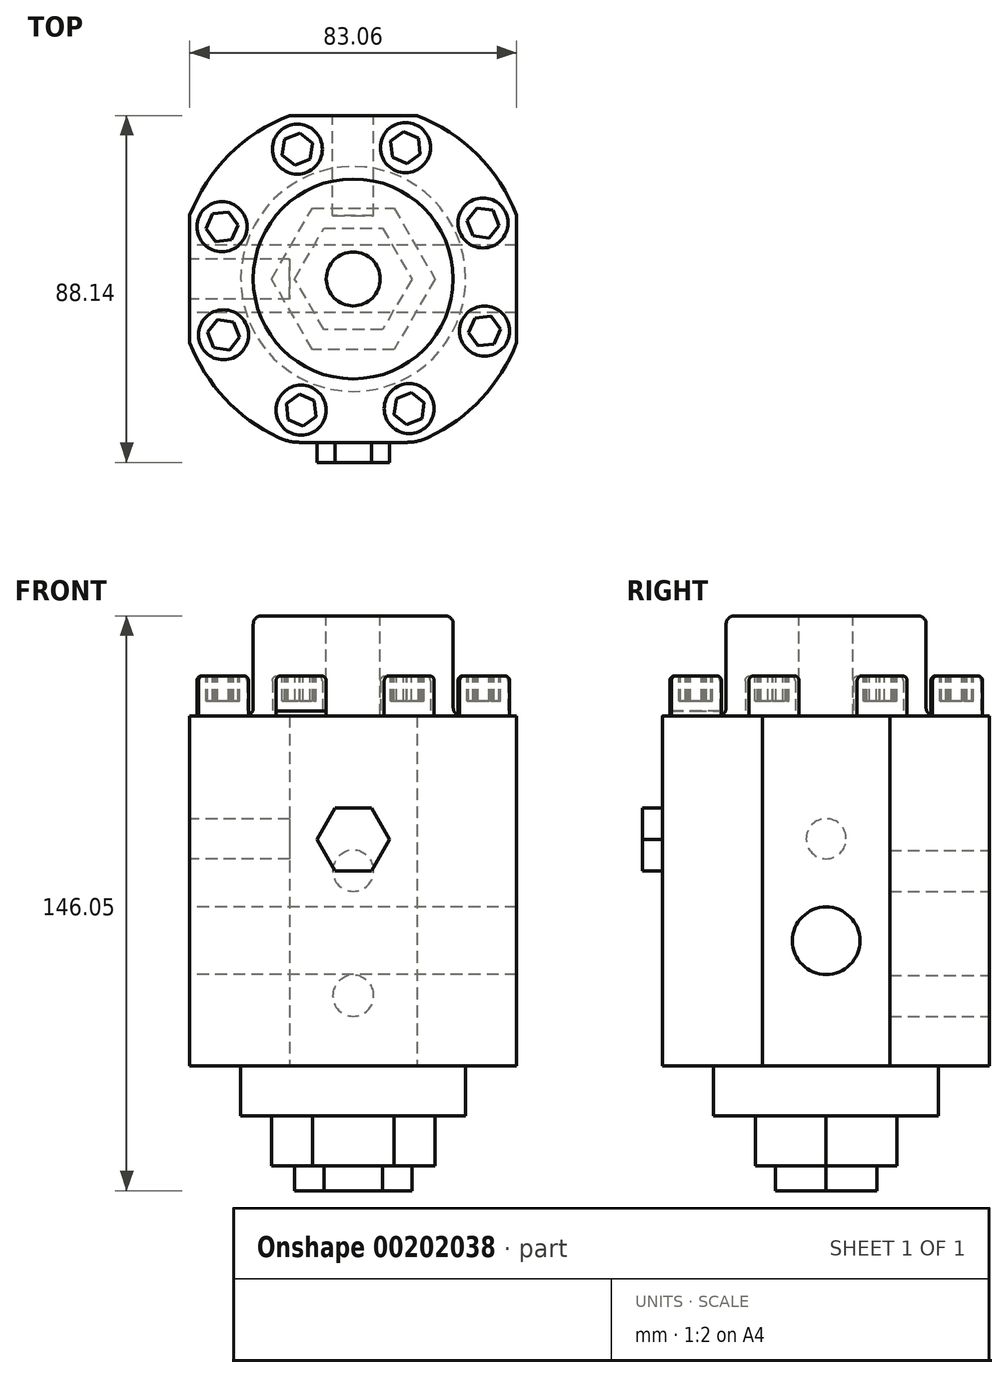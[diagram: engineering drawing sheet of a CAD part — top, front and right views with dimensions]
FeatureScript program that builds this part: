
annotation { "Feature Type Name" : "Feature", "Feature Type Description" : "" }
export const myFeature = defineFeature(function(context is Context, id is Id, definition is map)
    precondition{}
    {
        {
            var Q0;
            Q0=qCreatedBy(makeId("Top.planeOp"),FACE);
            var sketch = newSketch(context, id + "F0", { "sketchPlane" : qUnion([Q0])});
            skArc(sketch, "E0", {"start": v(41.53, 16.2) * mm, "mid": v(0, 44.58) * mm, "end": v(-41.53, 16.2) * mm});
            skLineSegment(sketch, "E1", {"start": v(41.53, 0) * mm, "end": v(41.53, 16.2) * mm});
            skLineSegment(sketch, "E2.MirrorCS", {"start": v(41.53, 0) * mm, "end": v(41.53, -16.2) * mm});
            skPoint(sketch, "E3.orphan", {"position": v(41.53, 44.35) * mm});
            skPoint(sketch, "E4.orphan", {"position": v(41.53, -44.35) * mm});
            skLineSegment(sketch, "E5.MirrorCS", {"start": v(-41.53, 0) * mm, "end": v(-41.53, -16.2) * mm});
            skLineSegment(sketch, "E6.MirrorCS", {"start": v(-41.53, 0) * mm, "end": v(-41.53, 16.2) * mm});
            skArc(sketch, "E7.trimOffspring", {"start": v(-41.53, -16.2) * mm, "mid": v(0, -44.58) * mm, "end": v(41.53, -16.2) * mm});
            skPoint(sketch, "E8.MirrorCS.end.orphan", {"position": v(-41.53, 0) * mm});
            skCircle(sketch, "E9", {"center": v(0, 0) * mm, "radius": 28.58 * mm});
            skCircle(sketch, "E10.cCircle", {"center": v(0, 0) * mm, "radius": 20.76 * mm, "construction": true});
            skLineSegment(sketch, "E10.0", {"start": v(10.38, 17.98) * mm, "end": v(20.76, 0) * mm});
            skLineSegment(sketch, "E10.1", {"start": v(20.76, 0) * mm, "end": v(10.38, -17.98) * mm});
            skLineSegment(sketch, "E10.2", {"start": v(10.38, -17.98) * mm, "end": v(-10.38, -17.98) * mm});
            skLineSegment(sketch, "E10.3", {"start": v(-10.38, -17.98) * mm, "end": v(-20.76, 0) * mm});
            skLineSegment(sketch, "E10.4", {"start": v(-20.76, 0) * mm, "end": v(-10.38, 17.98) * mm});
            skLineSegment(sketch, "E10.5", {"start": v(-10.38, 17.98) * mm, "end": v(10.38, 17.98) * mm});
            skCircle(sketch, "E11.cCircle", {"center": v(0, 0) * mm, "radius": 14.88 * mm, "construction": true});
            skLineSegment(sketch, "E11.0", {"start": v(7.44, 12.89) * mm, "end": v(14.88, 0) * mm});
            skLineSegment(sketch, "E11.1", {"start": v(14.88, 0) * mm, "end": v(7.44, -12.89) * mm});
            skLineSegment(sketch, "E11.2", {"start": v(7.44, -12.89) * mm, "end": v(-7.44, -12.89) * mm});
            skLineSegment(sketch, "E11.3", {"start": v(-7.44, -12.89) * mm, "end": v(-14.88, 0) * mm});
            skLineSegment(sketch, "E11.4", {"start": v(-14.88, 0) * mm, "end": v(-7.44, 12.89) * mm});
            skLineSegment(sketch, "E11.5", {"start": v(-7.44, 12.89) * mm, "end": v(7.44, 12.89) * mm});
            skLineSegment(sketch, "E12.1.0", {"start": v(0, -41.53) * mm, "end": v(-16.2, -41.53) * mm});
            skLineSegment(sketch, "E12.1.1", {"start": v(0, -41.53) * mm, "end": v(16.2, -41.53) * mm});
            skLineSegment(sketch, "E12.3.0", {"start": v(0, 41.53) * mm, "end": v(16.2, 41.53) * mm});
            skLineSegment(sketch, "E12.3.1", {"start": v(0, 41.53) * mm, "end": v(-16.2, 41.53) * mm});
            skSolve(sketch);
        }
        {
            var Q0;
            Q0=makeQuery(id+"F0.imprint","IMPRINT",FACE,{"disambiguationData":[TD([[makeQuery(id+"F0.imprint","IMPRINT",EDGE,{"derivedFrom":sQuery(id+"F0.wireOp",EDGE,"E0")}),1.0]])]});
            var Q1;
            Q1=makeQuery(id+"F0.imprint","IMPRINT",FACE,{"disambiguationData":[TD([[makeQuery(id+"F0.imprint","IMPRINT",EDGE,{"derivedFrom":sQuery(id+"F0.wireOp",EDGE,"E9")}),1.0]])]});
            var Q2;
            Q2=makeQuery(id+"F0.imprint","IMPRINT",FACE,{"disambiguationData":[TD([[makeQuery(id+"F0.imprint","IMPRINT",EDGE,{"derivedFrom":sQuery(id+"F0.wireOp",EDGE,"E10.0")}),-1.0]])]});
            var Q3;
            Q3=makeQuery(id+"F0.imprint","IMPRINT",FACE,{"disambiguationData":[TD([[makeQuery(id+"F0.imprint","IMPRINT",EDGE,{"derivedFrom":sQuery(id+"F0.wireOp",EDGE,"E11.0")}),-1.0]])]});
            extrude(context, id + "F1", {"entities" : qUnion([Q0, Q1, Q2, Q3]), "depth" : 88.9 * mm});
        }
        {
            var Q0;
            Q0=makeQuery(id+"F0.imprint","IMPRINT",FACE,{"disambiguationData":[TD([[makeQuery(id+"F0.imprint","IMPRINT",EDGE,{"derivedFrom":sQuery(id+"F0.wireOp",EDGE,"E9")}),1.0]])]});
            var Q1;
            Q1=makeQuery(id+"F0.imprint","IMPRINT",FACE,{"disambiguationData":[TD([[makeQuery(id+"F0.imprint","IMPRINT",EDGE,{"derivedFrom":sQuery(id+"F0.wireOp",EDGE,"E10.0")}),-1.0]])]});
            var Q2;
            Q2=makeQuery(id+"F0.imprint","IMPRINT",FACE,{"disambiguationData":[TD([[makeQuery(id+"F0.imprint","IMPRINT",EDGE,{"derivedFrom":sQuery(id+"F0.wireOp",EDGE,"E11.0")}),-1.0]])]});
            extrude(context, id + "F2", {"entities" : qUnion([Q0, Q1, Q2]), "operationType" : NewBodyOperationType.ADD, "oppositeDirection" : true, "depth" : 12.7 * mm});
        }
        {
            var Q0;
            Q0=makeQuery(id+"F0.imprint","IMPRINT",FACE,{"disambiguationData":[TD([[makeQuery(id+"F0.imprint","IMPRINT",EDGE,{"derivedFrom":sQuery(id+"F0.wireOp",EDGE,"E10.0")}),-1.0]])]});
            var Q1;
            Q1=makeQuery(id+"F0.imprint","IMPRINT",FACE,{"disambiguationData":[TD([[makeQuery(id+"F0.imprint","IMPRINT",EDGE,{"derivedFrom":sQuery(id+"F0.wireOp",EDGE,"E11.0")}),-1.0]])]});
            extrude(context, id + "F3", {"entities" : qUnion([Q0, Q1]), "operationType" : NewBodyOperationType.ADD, "oppositeDirection" : true, "depth" : 25.4 * mm});
        }
        {
            var Q0;
            Q0=makeQuery(id+"F0.imprint","IMPRINT",FACE,{"disambiguationData":[TD([[makeQuery(id+"F0.imprint","IMPRINT",EDGE,{"derivedFrom":sQuery(id+"F0.wireOp",EDGE,"E11.0")}),-1.0]])]});
            extrude(context, id + "F4", {"entities" : qUnion([Q0]), "operationType" : NewBodyOperationType.ADD, "oppositeDirection" : true, "depth" : 31.75 * mm});
        }
        {
            var Q0;
            Q0=makeQuery(id+"F4.opExtrude","CAP_FACE",FACE,{"disambiguationData":[OSD([sQuery(id+"F0.wireOp",EDGE,"E11.0"),sQuery(id+"F0.wireOp",EDGE,"E11.1"),sQuery(id+"F0.wireOp",EDGE,"E11.2"),sQuery(id+"F0.wireOp",EDGE,"E11.3"),sQuery(id+"F0.wireOp",EDGE,"E11.4"),sQuery(id+"F0.wireOp",EDGE,"E11.5")])],"isStart":false});
            cPlane(context, id + "F5", {"entities" : qUnion([Q0]), "cplaneType" : CPlaneType.OFFSET, "offset" : 63.5 * mm, "oppositeDirection" : true, "width" : 152.4 * mm, "height" : 152.4 * mm});
        }
        {
            var Q0;
            Q0=qCreatedBy(id+"F5.planeOp",FACE);
            var sketch = newSketch(context, id + "F6", { "sketchPlane" : qUnion([Q0])});
            skLineSegment(sketch, "E13", {"start": v(0, 0) * mm, "end": v(-41.53, 0) * mm});
            skSolve(sketch);
        }
        {
            var Q0;
            Q0=qCreatedBy(makeId("Front.planeOp"),FACE);
            var sketch = newSketch(context, id + "F7", { "sketchPlane" : qUnion([Q0])});
            skLineSegment(sketch, "E14", {"start": v(-41.53, 31.75) * mm, "end": v(-41.53, -2.92) * mm});
            skSolve(sketch);
        }
        {
            var Q0;
            Q0=sQuery(id+"F7.wireOp",EDGE,"E14");
            cPlane(context, id + "F8", {"entities" : qUnion([Q0]), "cplaneType" : CPlaneType.LINE_ANGLE, "offset" : 25.4 * mm, "angle" : 0 * degree, "width" : 152.4 * mm, "height" : 152.4 * mm});
        }
        {
            var Q0;
            Q0=qCreatedBy(id+"F8.planeOp",FACE);
            var sketch = newSketch(context, id + "F9", { "sketchPlane" : qUnion([Q0])});
            skCircle(sketch, "E15", {"center": v(0, 31.75) * mm, "radius": 8.57 * mm});
            skLineSegment(sketch, "E16", {"start": v(0, 31.75) * mm, "end": v(0, 57.66) * mm});
            skCircle(sketch, "E17", {"center": v(0, 57.66) * mm, "radius": 5.08 * mm});
            skSolve(sketch);
        }
        {
            var Q0;
            Q0=makeQuery(id+"F9.imprint","IMPRINT",FACE,{"disambiguationData":[TD([[makeQuery(id+"F9.imprint","IMPRINT",EDGE,{"derivedFrom":sQuery(id+"F9.wireOp",EDGE,"E15")}),1.0]])]});
            extrude(context, id + "F10", {"entities" : qUnion([Q0]), "operationType" : NewBodyOperationType.REMOVE, "oppositeDirection" : true, "depth" : 1092.2 * mm});
        }
        {
            var Q0;
            Q0=makeQuery(id+"F9.imprint","IMPRINT",FACE,{"disambiguationData":[TD([[makeQuery(id+"F9.imprint","IMPRINT",EDGE,{"derivedFrom":sQuery(id+"F9.wireOp",EDGE,"E17")}),1.0]])]});
            extrude(context, id + "F11", {"entities" : qUnion([Q0]), "operationType" : NewBodyOperationType.REMOVE, "oppositeDirection" : true, "depth" : 25.4 * mm});
        }
        {
            var Q0;
            Q0=makeQuery(id+"F1.opExtrude","CAP_FACE",FACE,{"disambiguationData":[OSD([sQuery(id+"F0.wireOp",EDGE,"E0"),sQuery(id+"F0.wireOp",EDGE,"E1"),sQuery(id+"F0.wireOp",EDGE,"E2.MirrorCS"),sQuery(id+"F0.wireOp",EDGE,"E5.MirrorCS"),sQuery(id+"F0.wireOp",EDGE,"E6.MirrorCS"),sQuery(id+"F0.wireOp",EDGE,"E7.trimOffspring")])],"isStart":false});
            var sketch = newSketch(context, id + "F12", { "sketchPlane" : qUnion([Q0])});
            skCircle(sketch, "E18", {"center": v(0, 0) * mm, "radius": 25.4 * mm});
            skSolve(sketch);
        }
        {
            var Q0;
            Q0=qSketchRegion(id+"F12",true);
            extrude(context, id + "F13", {"entities" : qUnion([Q0]), "operationType" : NewBodyOperationType.ADD, "depth" : 25.4 * mm});
        }
        {
            var Q0;
            Q0=makeQuery(id+"F13.opExtrude","SWEPT_FACE",FACE,{"disambiguationData":[OSD([sQuery(id+"F12.wireOp",EDGE,"E18")])]});
            fillet(context, id + "F14", {"entities" : qUnion([Q0]), "radius" : 2.03 * mm, "tangentPropagation" : true, "allowEdgeOverflow" : false});
        }
        {
            var Q0;
            Q0=makeQuery(id+"F1.opExtrude","SWEPT_FACE",FACE,{"disambiguationData":[OSD([sQuery(id+"F0.wireOp",EDGE,"E12.1.0"),sQuery(id+"F0.wireOp",EDGE,"E12.1.1")])]});
            var sketch = newSketch(context, id + "F15", { "sketchPlane" : qUnion([Q0])});
            skLineSegment(sketch, "E19", {"start": v(0, 88.9) * mm, "end": v(0, 57.48) * mm});
            skPoint(sketch, "E19.endSnap0", {"position": v(0, 88.9) * mm});
            skCircle(sketch, "E20.cCircle", {"center": v(0, 57.48) * mm, "radius": 9.18 * mm, "construction": true});
            skLineSegment(sketch, "E20.0", {"start": v(4.6, 49.53) * mm, "end": v(-4.6, 49.53) * mm});
            skLineSegment(sketch, "E20.1", {"start": v(-4.6, 49.53) * mm, "end": v(-9.18, 57.48) * mm});
            skLineSegment(sketch, "E20.2", {"start": v(-9.18, 57.48) * mm, "end": v(-4.6, 65.43) * mm});
            skLineSegment(sketch, "E20.3", {"start": v(-4.6, 65.43) * mm, "end": v(4.6, 65.43) * mm});
            skLineSegment(sketch, "E20.4", {"start": v(4.6, 65.43) * mm, "end": v(9.18, 57.48) * mm});
            skLineSegment(sketch, "E20.5", {"start": v(9.18, 57.48) * mm, "end": v(4.6, 49.53) * mm});
            skSolve(sketch);
        }
        {
            var Q0;
            Q0=qSketchRegion(id+"F15",true);
            extrude(context, id + "F16", {"entities" : qUnion([Q0]), "operationType" : NewBodyOperationType.ADD, "depth" : 5.08 * mm});
        }
        {
            var Q0;
            Q0=makeQuery(id+"F13.opExtrude","CAP_FACE",FACE,{"disambiguationData":[OSD([sQuery(id+"F12.wireOp",EDGE,"E18")])],"isStart":false});
            var sketch = newSketch(context, id + "F17", { "sketchPlane" : qUnion([Q0])});
            skCircle(sketch, "E21", {"center": v(0, 0) * mm, "radius": 6.86 * mm});
            skSolve(sketch);
        }
        {
            var Q0;
            Q0=qSketchRegion(id+"F17",true);
            extrude(context, id + "F18", {"entities" : qUnion([Q0]), "operationType" : NewBodyOperationType.REMOVE, "oppositeDirection" : true, "depth" : 25.4 * mm});
        }
        {
            var Q0;
            Q0=makeQuery(id+"F1.opExtrude","SWEPT_FACE",FACE,{"disambiguationData":[OSD([sQuery(id+"F0.wireOp",EDGE,"E12.3.0"),sQuery(id+"F0.wireOp",EDGE,"E12.3.1")])]});
            var sketch = newSketch(context, id + "F19", { "sketchPlane" : qUnion([Q0])});
            skLineSegment(sketch, "E22", {"start": v(0, 0) * mm, "end": v(0, 17.78) * mm});
            skCircle(sketch, "E23", {"center": v(0, 17.78) * mm, "radius": 5.2 * mm});
            skLineSegment(sketch, "E24", {"start": v(0, 17.78) * mm, "end": v(0, 49.53) * mm});
            skCircle(sketch, "E25", {"center": v(0, 49.53) * mm, "radius": 5.2 * mm});
            skSolve(sketch);
        }
        {
            var Q0;
            Q0=makeQuery(id+"F19.imprint","IMPRINT",FACE,{"disambiguationData":[TD([[makeQuery(id+"F19.imprint","IMPRINT",EDGE,{"derivedFrom":sQuery(id+"F19.wireOp",EDGE,"E25")}),1.0]])]});
            var Q1;
            {var subQ0=sQuery(id+"F19.wireOp",EDGE,"E24");var subQ1=sQuery(id+"F19.wireOp",EDGE,"E22");var subQ2=makeQuery(id+"F19.imprint","INTERSECT",VERTEX,{"derivedFrom":[subQ1,subQ0]});Q1=makeQuery(id+"F19.imprint","IMPRINT",FACE,{"disambiguationData":[TD([[makeQuery(id+"F19.imprint","IMPRINT",EDGE,{"disambiguationData":[TD([[subQ2,1.0]])],"derivedFrom":subQ1}),-1.0]])]});}
            var Q2;
            {var subQ0=sQuery(id+"F19.wireOp",EDGE,"E24");var subQ1=sQuery(id+"F19.wireOp",EDGE,"E22");var subQ2=makeQuery(id+"F19.imprint","INTERSECT",VERTEX,{"derivedFrom":[subQ1,subQ0]});Q2=makeQuery(id+"F19.imprint","IMPRINT",FACE,{"disambiguationData":[TD([[makeQuery(id+"F19.imprint","IMPRINT",EDGE,{"disambiguationData":[TD([[subQ2,1.0]])],"derivedFrom":subQ1}),1.0]])]});}
            extrude(context, id + "F20", {"entities" : qUnion([Q0, Q1, Q2]), "operationType" : NewBodyOperationType.REMOVE, "oppositeDirection" : true, "depth" : 25.4 * mm});
        }
        {
            var Q0;
            Q0=makeQuery(id+"F1.opExtrude","SWEPT_EDGE",EDGE,{"disambiguationData":[OSD([sQuery(id+"F0.wireOp",EDGE,"E7.trimOffspring"),sQuery(id+"F0.wireOp",EDGE,"E12.1.0")])]});
            var Q1;
            Q1=makeQuery(id+"F1.opExtrude","SWEPT_EDGE",EDGE,{"disambiguationData":[OSD([sQuery(id+"F0.wireOp",EDGE,"E7.trimOffspring"),sQuery(id+"F0.wireOp",EDGE,"E12.1.1")])]});
            fillet(context, id + "F21", {"entities" : qUnion([Q0, Q1]), "radius" : 12.7 * mm, "tangentPropagation" : true, "allowEdgeOverflow" : false});
        }
        {
            var Q0;
            Q0=makeQuery(id+"F1.opExtrude","CAP_FACE",FACE,{"disambiguationData":[OSD([sQuery(id+"F0.wireOp",EDGE,"E0"),sQuery(id+"F0.wireOp",EDGE,"E5.MirrorCS"),sQuery(id+"F0.wireOp",EDGE,"E6.MirrorCS"),sQuery(id+"F0.wireOp",EDGE,"E7.trimOffspring"),sQuery(id+"F0.wireOp",EDGE,"E12.1.0"),sQuery(id+"F0.wireOp",EDGE,"E12.1.1"),sQuery(id+"F0.wireOp",EDGE,"E2.MirrorCS"),sQuery(id+"F0.wireOp",EDGE,"E1"),sQuery(id+"F0.wireOp",EDGE,"E12.3.0"),sQuery(id+"F0.wireOp",EDGE,"E12.3.1")])],"isStart":false});
            var sketch = newSketch(context, id + "F22", { "sketchPlane" : qUnion([Q0])});
            skLineSegment(sketch, "E26", {"start": v(0, 0) * mm, "end": v(-16.38, -41.22) * mm});
            skLineSegment(sketch, "E27", {"start": v(-16.38, -41.22) * mm, "end": v(-10.13, -25.5) * mm});
            skLineSegment(sketch, "E28", {"start": v(-10.13, -25.5) * mm, "end": v(-13.25, -33.36) * mm});
            skCircle(sketch, "E29", {"center": v(-13.25, -33.36) * mm, "radius": 6.35 * mm});
            skCircle(sketch, "E30", {"center": v(-13.25, -33.36) * mm, "radius": 7.94 * mm});
            skCircle(sketch, "E31.cCircle", {"center": v(-13.25, -33.36) * mm, "radius": 3.96 * mm, "construction": true});
            skLineSegment(sketch, "E31.0", {"start": v(-10.15, -30.9) * mm, "end": v(-9.57, -34.82) * mm});
            skLineSegment(sketch, "E31.1", {"start": v(-9.57, -34.82) * mm, "end": v(-12.68, -37.28) * mm});
            skLineSegment(sketch, "E31.2", {"start": v(-12.68, -37.28) * mm, "end": v(-16.36, -35.81) * mm});
            skLineSegment(sketch, "E31.3", {"start": v(-16.36, -35.81) * mm, "end": v(-16.93, -31.9) * mm});
            skLineSegment(sketch, "E31.4", {"start": v(-16.93, -31.9) * mm, "end": v(-13.83, -29.44) * mm});
            skLineSegment(sketch, "E31.5", {"start": v(-13.83, -29.44) * mm, "end": v(-10.15, -30.9) * mm});
            skSolve(sketch);
        }
        {
            var Q0;
            {var subQ0=sQuery(id+"F22.wireOp",EDGE,"E30");var subQ1=sQuery(id+"F22.wireOp",EDGE,"E27");var subQ2=makeQuery(id+"F22.imprint","INTERSECT",VERTEX,{"derivedFrom":[subQ1,subQ0]});Q0=makeQuery(id+"F22.imprint","IMPRINT",FACE,{"disambiguationData":[TD([[makeQuery(id+"F22.imprint","IMPRINT",EDGE,{"disambiguationData":[TD([[subQ2,-1.0]])],"derivedFrom":subQ1}),-1.0]])]});}
            var Q1;
            {var subQ0=sQuery(id+"F22.wireOp",EDGE,"E30");var subQ1=sQuery(id+"F22.wireOp",EDGE,"E27");var subQ2=makeQuery(id+"F22.imprint","INTERSECT",VERTEX,{"derivedFrom":[subQ1,subQ0]});Q1=makeQuery(id+"F22.imprint","IMPRINT",FACE,{"disambiguationData":[TD([[makeQuery(id+"F22.imprint","IMPRINT",EDGE,{"disambiguationData":[TD([[subQ2,-1.0]])],"derivedFrom":subQ1}),1.0]])]});}
            var Q2;
            {var subQ0=sQuery(id+"F22.wireOp",EDGE,"E31.3");Q2=makeQuery(id+"F22.imprint","IMPRINT",FACE,{"disambiguationData":[TD([[makeQuery(id+"F22.imprint","IMPRINT",EDGE,{"derivedFrom":subQ0}),1.0]])]});}
            var Q3;
            {var subQ0=sQuery(id+"F22.wireOp",EDGE,"E31.0");Q3=makeQuery(id+"F22.imprint","IMPRINT",FACE,{"disambiguationData":[TD([[makeQuery(id+"F22.imprint","IMPRINT",EDGE,{"derivedFrom":subQ0}),1.0]])]});}
            var Q4;
            {var subQ6=sQuery(id+"F22.wireOp",EDGE,"E31.0");Q4=makeQuery(id+"F22.imprint","IMPRINT",FACE,{"disambiguationData":[TD([[makeQuery(id+"F22.imprint","IMPRINT",EDGE,{"derivedFrom":subQ6}),-1.0]])]});}
            var Q5;
            {var subQ0=sQuery(id+"F22.wireOp",EDGE,"E31.3");Q5=makeQuery(id+"F22.imprint","IMPRINT",FACE,{"disambiguationData":[TD([[makeQuery(id+"F22.imprint","IMPRINT",EDGE,{"derivedFrom":subQ0}),-1.0]])]});}
            extrude(context, id + "F23", {"entities" : qUnion([Q0, Q1, Q2, Q3, Q4, Q5]), "depth" : 1.27 * mm});
        }
        {
            var Q0;
            {var subQ0=sQuery(id+"F22.wireOp",EDGE,"E31.3");Q0=makeQuery(id+"F22.imprint","IMPRINT",FACE,{"disambiguationData":[TD([[makeQuery(id+"F22.imprint","IMPRINT",EDGE,{"derivedFrom":subQ0}),1.0]])]});}
            var Q1;
            {var subQ0=sQuery(id+"F22.wireOp",EDGE,"E31.0");Q1=makeQuery(id+"F22.imprint","IMPRINT",FACE,{"disambiguationData":[TD([[makeQuery(id+"F22.imprint","IMPRINT",EDGE,{"derivedFrom":subQ0}),1.0]])]});}
            var Q2;
            {var subQ0=sQuery(id+"F22.wireOp",EDGE,"E31.3");Q2=makeQuery(id+"F22.imprint","IMPRINT",FACE,{"disambiguationData":[TD([[makeQuery(id+"F22.imprint","IMPRINT",EDGE,{"derivedFrom":subQ0}),-1.0]])]});}
            var Q3;
            {var subQ6=sQuery(id+"F22.wireOp",EDGE,"E31.0");Q3=makeQuery(id+"F22.imprint","IMPRINT",FACE,{"disambiguationData":[TD([[makeQuery(id+"F22.imprint","IMPRINT",EDGE,{"derivedFrom":subQ6}),-1.0]])]});}
            extrude(context, id + "F24", {"entities" : qUnion([Q0, Q1, Q2, Q3]), "depth" : 10.16 * mm});
        }
        {
            var Q0;
            Q0=makeQuery(id+"F24.opExtrude","CAP_FACE",FACE,{"disambiguationData":[OSD([sQuery(id+"F22.wireOp",EDGE,"E29")])],"isStart":false});
            var sketch = newSketch(context, id + "F25", { "sketchPlane" : qUnion([Q0])});
            skCircle(sketch, "E32.cCircle", {"center": v(-13.25, -33.36) * mm, "radius": 4.1 * mm, "construction": true});
            skLineSegment(sketch, "E32.0", {"start": v(-9.95, -30.94) * mm, "end": v(-9.5, -35.01) * mm});
            skLineSegment(sketch, "E32.1", {"start": v(-9.5, -35.01) * mm, "end": v(-12.82, -37.43) * mm});
            skLineSegment(sketch, "E32.2", {"start": v(-12.82, -37.43) * mm, "end": v(-16.56, -35.77) * mm});
            skLineSegment(sketch, "E32.3", {"start": v(-16.56, -35.77) * mm, "end": v(-17, -31.7) * mm});
            skLineSegment(sketch, "E32.4", {"start": v(-17, -31.7) * mm, "end": v(-13.7, -29.29) * mm});
            skLineSegment(sketch, "E32.5", {"start": v(-13.7, -29.29) * mm, "end": v(-9.95, -30.94) * mm});
            skSolve(sketch);
        }
        {
            var Q0;
            Q0=qSketchRegion(id+"F25",true);
            extrude(context, id + "F26", {"entities" : qUnion([Q0]), "operationType" : NewBodyOperationType.REMOVE, "oppositeDirection" : true, "depth" : 6.35 * mm});
        }
        {
            var Q0;
            Q0=makeQuery(id+"F24.opExtrude","CAP_EDGE",EDGE,{"disambiguationData":[OSD([sQuery(id+"F22.wireOp",EDGE,"E29")])],"isStart":false});
            fillet(context, id + "F27", {"entities" : qUnion([Q0]), "radius" : 1.27 * mm, "tangentPropagation" : true, "allowEdgeOverflow" : false});
        }
        {
            var Q0;
            Q0=makeQuery(id+"F24.opExtrude","SWEPT_BODY",BODY,{"disambiguationData":[OSD([sQuery(id+"F22.wireOp",EDGE,"E29")])]});
            var Q1;
            Q1=makeQuery(id+"F23.opExtrude","SWEPT_BODY",BODY,{"disambiguationData":[OSD([sQuery(id+"F22.wireOp",EDGE,"E30")])]});
            var Q2;
            Q2=makeQuery(id+"F18.boolean.opBoolean","COPY",FACE,{"derivedFrom":makeQuery(id+"F18.opExtrude","SWEPT_FACE",FACE,{"disambiguationData":[OSD([sQuery(id+"F17.wireOp",EDGE,"E21")])]})});
            circularPattern(context, id + "F28", {"entities" : qUnion([Q0, Q1]), "axis" : qUnion([Q2]), "angle" : 360 * degree, "instanceCount" : 8, "equalSpace" : true});
        }
    });
